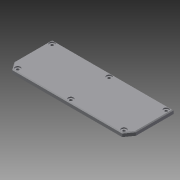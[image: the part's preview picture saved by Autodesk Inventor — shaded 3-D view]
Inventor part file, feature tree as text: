
AUTODESK INVENTOR PART (.ipt)
format: ipt  version: 2014 (Build 180170000, 170)  size: 125,440 bytes
history: native  units: mm
features: sketch x2, extrude x1, hole x1, chamfer x1, reference x1
ambient origin geometry x8: Origin, YZ Plane, XZ Plane, XY Plane, X Axis, Y Axis, Z Axis, Center Point
bodies: Solid1 (feature_tree)
feature tree (6):
  extrude  "Extrusion1"  Depth=5.0mm TaperAngle=0.0deg
  hole  "Hole1"  [1 undecoded]
  chamfer  "Chamfer1"  [1 undecoded]
  sketch  "Sketch1"  dims[d0=0.15mm d1=5.0mm d2=0.0mm]
  reference  "Reference1"
  sketch  "Sketch2"  dims[d3=3.5mm d4=6.0mm d5=7.0mm d6=1.5mm d7=90.0deg d8=8.0mm d9=20.594885mm d10=1.0mm d11=2.0mm d12=45.0deg]
note: 2 required parameter values undecoded (feature->parameter linkage not recoverable at this tier; creation-order binding heuristic only, values carry confidence <= 0.55)
